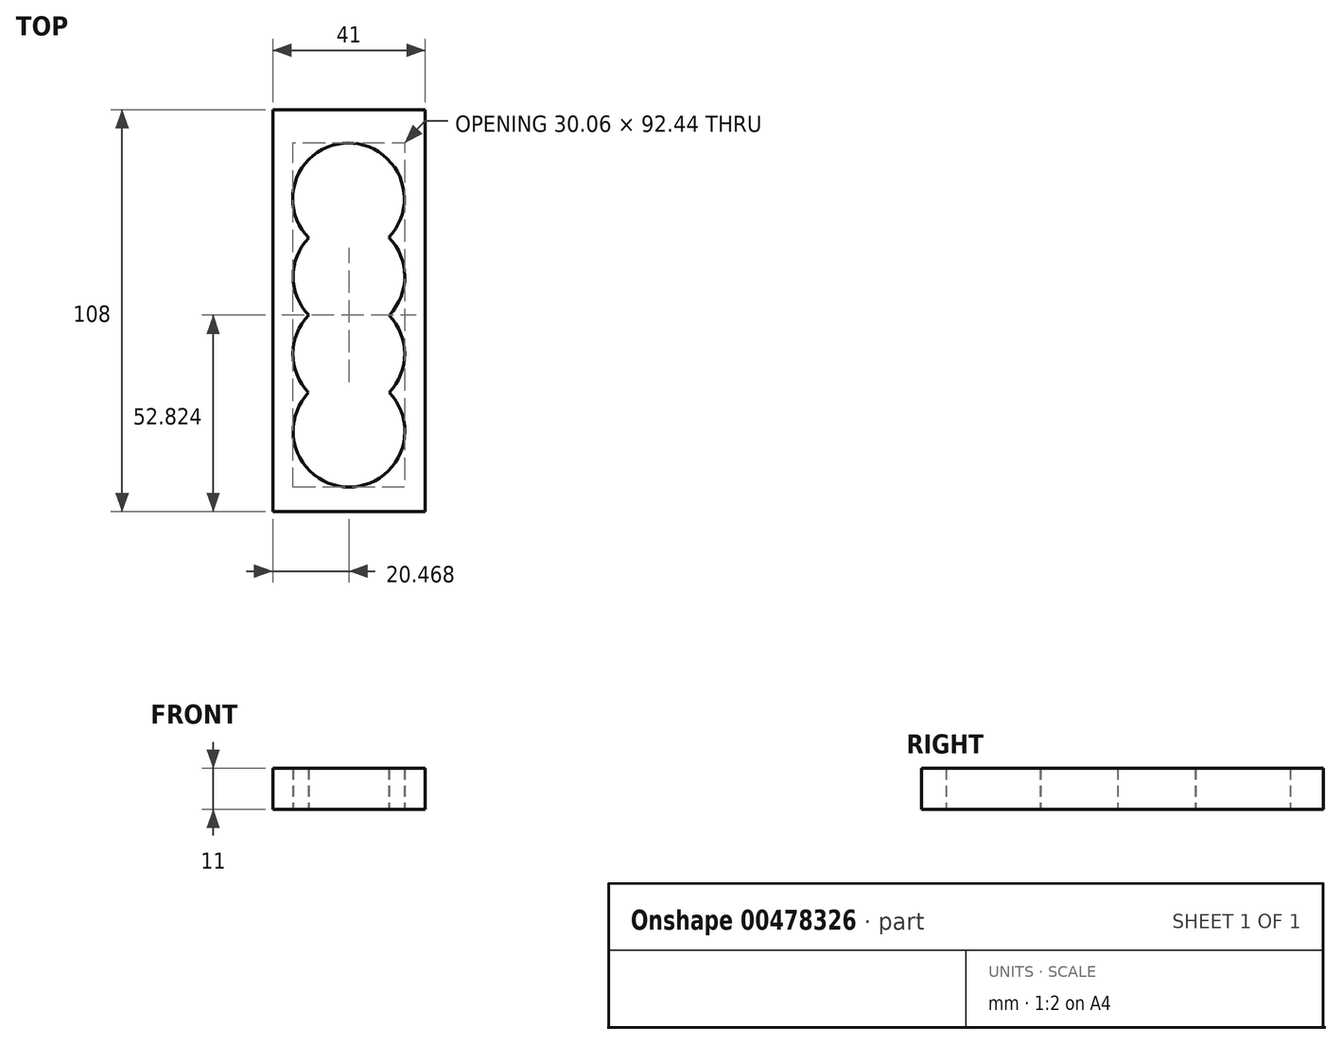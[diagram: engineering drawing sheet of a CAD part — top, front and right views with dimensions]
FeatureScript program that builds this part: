
annotation { "Feature Type Name" : "Feature", "Feature Type Description" : "" }
export const myFeature = defineFeature(function(context is Context, id is Id, definition is map)
    precondition{}
    {
        {
            var Q0;
            Q0=qCreatedBy(makeId("Top.planeOp"),FACE);
            var sketch = newSketch(context, id + "F0", { "sketchPlane" : qUnion([Q0])});
            skLineSegment(sketch, "E0", {"start": v(-0.18, 42.76) * mm, "end": v(0, -38.86) * mm, "construction": true});
            skCircle(sketch, "E1", {"center": v(-0.06, -12.62) * mm, "radius": 9 * mm});
            skCircle(sketch, "E2", {"center": v(-0.1, 8.22) * mm, "radius": 9 * mm});
            skCircle(sketch, "E3", {"center": v(-0.15, 29.04) * mm, "radius": 9 * mm});
            skPoint(sketch, "E4.oppositeSnap0", {"position": v(8.9, -24.62) * mm});
            skPoint(sketch, "E5.endSnap0", {"position": v(-13.1, -24.62) * mm});
            skCircle(sketch, "E6", {"center": v(10.35, 29.04) * mm, "radius": 1.25 * mm});
            skCircle(sketch, "E7", {"center": v(10.35, 8.22) * mm, "radius": 1.25 * mm});
            skCircle(sketch, "E8", {"center": v(10.35, -12.62) * mm, "radius": 1.25 * mm});
            skCircle(sketch, "E9.MirrorC", {"center": v(-10.65, 29) * mm, "radius": 1.25 * mm});
            skCircle(sketch, "E10.MirrorC", {"center": v(-10.56, 8.18) * mm, "radius": 1.25 * mm});
            skCircle(sketch, "E11.MirrorC", {"center": v(-10.47, -12.67) * mm, "radius": 1.25 * mm});
            skCircle(sketch, "E12", {"center": v(10.35, -33.38) * mm, "radius": 1.25 * mm});
            skCircle(sketch, "E13", {"center": v(-10.47, -33.43) * mm, "radius": 1.25 * mm});
            skCircle(sketch, "E14", {"center": v(-0.02, -33.4) * mm, "radius": 9 * mm});
            skLineSegment(sketch, "E15", {"start": v(-0.1, 8.22) * mm, "end": v(-23.14, 8.17) * mm, "construction": true});
            skLineSegment(sketch, "E16", {"start": v(-0.06, -12.62) * mm, "end": v(-20.8, -12.67) * mm, "construction": true});
            skLineSegment(sketch, "E17", {"start": v(12.8, -12.1) * mm, "end": v(12.8, -12.85) * mm});
            skLineSegment(sketch, "E18", {"start": v(-13.03, -12.27) * mm, "end": v(-13.03, -12.78) * mm});
            skLineSegment(sketch, "E19", {"start": v(-13.37, 8.31) * mm, "end": v(-13.37, 8.08) * mm});
            skLineSegment(sketch, "E20", {"start": v(13.19, 8.34) * mm, "end": v(13.19, 8.17) * mm});
            skCircle(sketch, "E21", {"center": v(-10.47, -12.67) * mm, "radius": 2.25 * mm});
            skCircle(sketch, "E22", {"center": v(10.35, -12.62) * mm, "radius": 2.25 * mm});
            skPoint(sketch, "E23.startSnap0", {"position": v(-9, -2.31) * mm});
            skPoint(sketch, "E23.endSnap0", {"position": v(-9.76, -22) * mm});
            skPoint(sketch, "E24.startSnap0", {"position": v(-9.04, 18.63) * mm});
            skCircle(sketch, "E25", {"center": v(-0.15, 29.04) * mm, "radius": 15 * mm});
            skCircle(sketch, "E26", {"center": v(-0.02, -33.4) * mm, "radius": 15 * mm});
            skCircle(sketch, "E27", {"center": v(-10.56, 8.18) * mm, "radius": 2.5 * mm});
            skCircle(sketch, "E28", {"center": v(10.35, 8.22) * mm, "radius": 2.5 * mm});
            skCircle(sketch, "E29", {"center": v(10.35, 29.04) * mm, "radius": 2.5 * mm});
            skCircle(sketch, "E30", {"center": v(-10.65, 29) * mm, "radius": 2.5 * mm});
            skCircle(sketch, "E31", {"center": v(-10.47, -33.43) * mm, "radius": 2.5 * mm});
            skCircle(sketch, "E32", {"center": v(10.35, -33.38) * mm, "radius": 2.5 * mm});
            skCircle(sketch, "E33", {"center": v(-0.06, -12.62) * mm, "radius": 15 * mm});
            skCircle(sketch, "E34", {"center": v(0, 8.16) * mm, "radius": 15 * mm});
            skLineSegment(sketch, "E35.bottom", {"start": v(-20.5, 53) * mm, "end": v(20.5, 53) * mm});
            skLineSegment(sketch, "E35.top", {"start": v(-20.5, -55) * mm, "end": v(20.5, -55) * mm});
            skLineSegment(sketch, "E35.left", {"start": v(-20.5, 53) * mm, "end": v(-20.5, -55) * mm});
            skLineSegment(sketch, "E35.right", {"start": v(20.5, 53) * mm, "end": v(20.5, -55) * mm});
            skSolve(sketch);
        }
        {
            var Q0;
            Q0=qSketchRegion(id+"F0",true);
            extrude(context, id + "F1", {"entities" : qUnion([Q0]), "depth" : 11 * mm});
        }
    });
